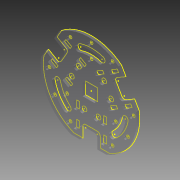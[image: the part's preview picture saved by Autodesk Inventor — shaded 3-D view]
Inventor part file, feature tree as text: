
AUTODESK INVENTOR PART (.ipt)
format: ipt  version: 2015 (Build 190159000, 159)  size: 448,512 bytes
history: native  units: mm
features: sketch x8, extrude x7, projected_geometry x4, pattern_circular x3, fillet x1
ambient origin geometry x8: Origin, YZ Plane, XZ Plane, XY Plane, X Axis, Y Axis, Z Axis, Center Point
bodies: Solid1 (feature_tree)
feature tree (23):
  extrude  "Extrusion1"  Depth=47.907mm
  sketch  "Sketch2"  dims[d2=120.0deg d3=120.0deg]
  sketch  "Sketch3"  dims[d4=47.907mm d5=47.907mm]
  extrude  "Extrusion2"  TaperAngle=120.0deg  [1 undecoded]
  extrude  "Extrusion3"  Depth=47.907mm
  extrude  "Extrusion4"  Depth=51.5mm
  extrude  "Extrusion5"  Depth=3.0mm TaperAngle=0.0deg
  pattern_circular  "Circular Pattern1"  [2 undecoded]
  extrude  "Extrusion6"  Depth=7.0mm
  extrude  "Extrusion7"  Depth=7.0mm
  pattern_circular  "Circular Pattern2"  [2 undecoded]
  fillet  "Fillet1"  Radius=7.0mm
  pattern_circular  "Circular Pattern3"  [2 undecoded]
  sketch  "Sketch9"  dims[d13=20.006mm d14=15.0mm d15=7.0mm d16=7.0mm d17=11.0mm d18=7.0mm d19=32.0mm d20=3.0mm d21=3.0mm d22=3.0mm d23=0.0mm d24=3.0mm d25=0.0mm d26=18.5mm d28=14.0mm d29=3.0mm d30=0.0mm d31=12.8mm d32=12.8mm d33=3.0mm d34=0.0mm d35=30.0mm d36=360.0deg d38=3.0mm d39=3.0mm d40=3.0mm d41=120.0deg d42=120.0deg d43=90.0mm d44=60.0mm d45=3.0mm d46=3.0mm d47=3.0mm d48=3.0mm d49=0.0mm d50=7.330383mm d51=7.330383mm d52=6.0mm d53=34.0mm d54=3.0mm d55=0.0mm d56=30.0mm d57=360.0deg d59=3.0mm d60=30.0mm d61=360.0deg d63=3.0mm d64=3.0mm d65=3.0mm d66=3.0mm d67=30.0deg d68=30.0deg d69=30.0deg d70=30.0deg d71=30.0deg d72=30.0deg d73=3.0mm d74=3.0mm]
  sketch  "Sketch1"  dims[d0=100.0mm d1=47.907mm]
  projected_geometry  "Projected Loop1"
  sketch  "Sketch4"  dims[d6=51.5mm d7=51.5mm]
  sketch  "Sketch5"  dims[d8=51.5mm d9=3.0mm d10=0.0mm]
  sketch  "Sketch6"  dims[d11=5.0mm]
  projected_geometry  "Projected Loop2"
  sketch  "Sketch7"  dims[d12=5.0mm]
  projected_geometry  "Projected Loop3"
  projected_geometry  "Projected Loop5"
note: 7 required parameter values undecoded (feature->parameter linkage not recoverable at this tier; creation-order binding heuristic only, values carry confidence <= 0.55)
